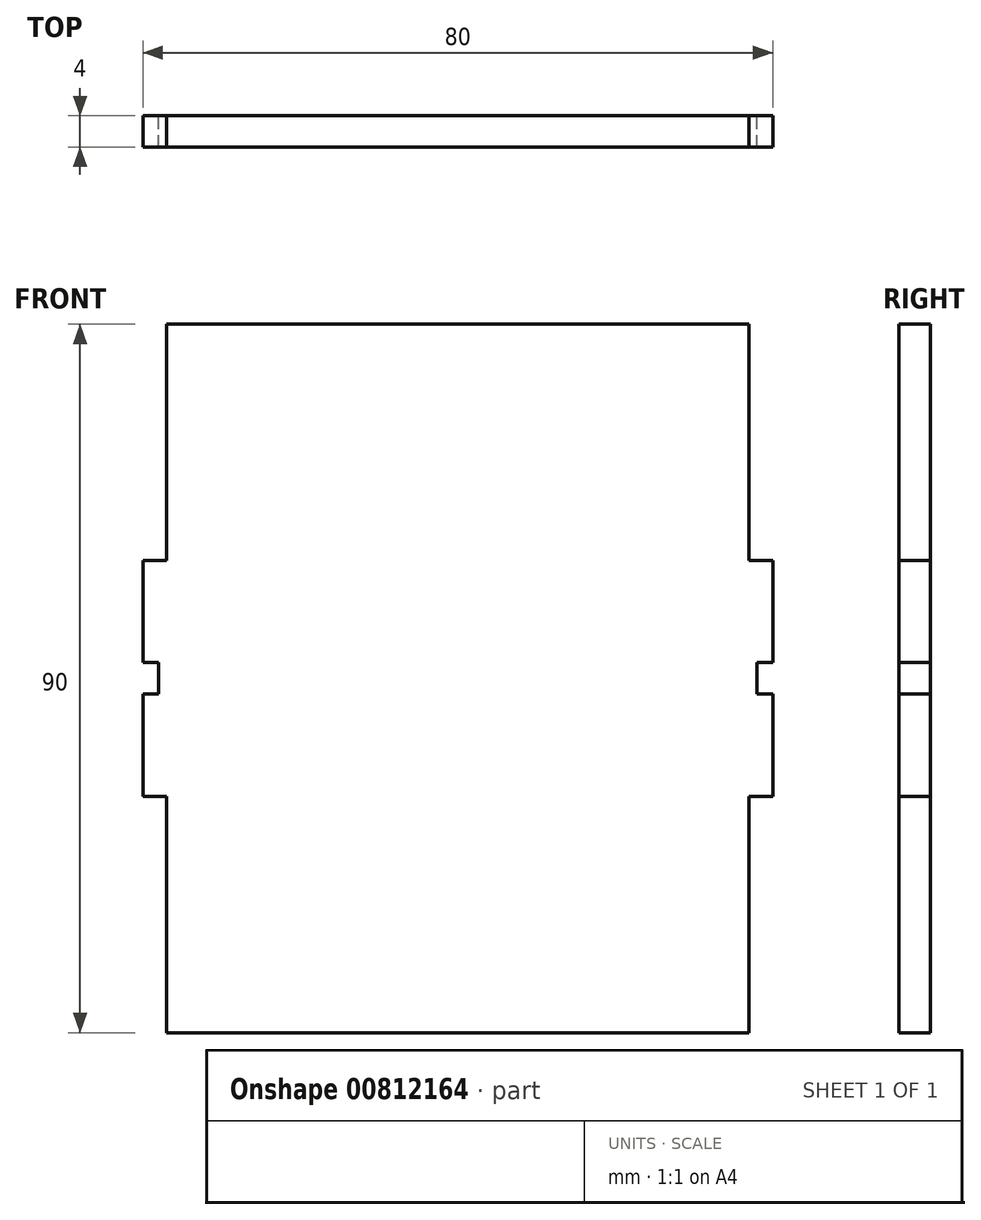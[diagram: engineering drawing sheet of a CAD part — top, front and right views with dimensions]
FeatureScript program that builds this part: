
annotation { "Feature Type Name" : "Feature", "Feature Type Description" : "" }
export const myFeature = defineFeature(function(context is Context, id is Id, definition is map)
    precondition{}
    {
        {
            var Q0;
            Q0=qCreatedBy(makeId("Front.planeOp"),FACE);
            var sketch = newSketch(context, id + "F0", { "sketchPlane" : qUnion([Q0])});
            skLineSegment(sketch, "E0", {"start": v(40, 2) * mm, "end": v(40, 15) * mm});
            skLineSegment(sketch, "E1", {"start": v(37, 45) * mm, "end": v(-37, 45) * mm});
            skLineSegment(sketch, "E2", {"start": v(-40, 15) * mm, "end": v(-40, 2) * mm});
            skLineSegment(sketch, "E3", {"start": v(-37, -45) * mm, "end": v(37, -45) * mm});
            skLineSegment(sketch, "E4", {"start": v(40, -15) * mm, "end": v(40, -2) * mm});
            skLineSegment(sketch, "E5.0", {"start": v(37, 15) * mm, "end": v(40, 15) * mm});
            skLineSegment(sketch, "E6.0", {"start": v(37, -15) * mm, "end": v(40, -15) * mm});
            skLineSegment(sketch, "E7.MirrorCS", {"start": v(37, 15) * mm, "end": v(37, 45) * mm});
            skLineSegment(sketch, "E8.MirrorCS", {"start": v(37, -15) * mm, "end": v(37, -45) * mm});
            skLineSegment(sketch, "E9.0", {"start": v(38, -2) * mm, "end": v(40, -2) * mm});
            skLineSegment(sketch, "E10.0", {"start": v(38, -2) * mm, "end": v(38, 0) * mm});
            skLineSegment(sketch, "E11.MirrorCS", {"start": v(38, 2) * mm, "end": v(38, 0) * mm});
            skLineSegment(sketch, "E12.MirrorCS", {"start": v(38, 2) * mm, "end": v(40, 2) * mm});
            skPoint(sketch, "E13.start.orphan", {"position": v(0, 0) * mm});
            skLineSegment(sketch, "E14.MirrorCS", {"start": v(-37, 15) * mm, "end": v(-40, 15) * mm});
            skLineSegment(sketch, "E15.MirrorCS", {"start": v(-37, -15) * mm, "end": v(-40, -15) * mm});
            skLineSegment(sketch, "E16.MirrorCS", {"start": v(-38, 2) * mm, "end": v(-40, 2) * mm});
            skLineSegment(sketch, "E17.MirrorCS", {"start": v(-38, -2) * mm, "end": v(-40, -2) * mm});
            skLineSegment(sketch, "E18.MirrorCS", {"start": v(-38, -2) * mm, "end": v(-38, 0) * mm});
            skLineSegment(sketch, "E19.MirrorCS", {"start": v(-38, 2) * mm, "end": v(-38, 0) * mm});
            skLineSegment(sketch, "E20.MirrorCS", {"start": v(-40, 2) * mm, "end": v(-40, 15) * mm});
            skLineSegment(sketch, "E21.MirrorCS", {"start": v(-40, -15) * mm, "end": v(-40, -2) * mm});
            skLineSegment(sketch, "E22.MirrorCS", {"start": v(-37, -15) * mm, "end": v(-37, -45) * mm});
            skLineSegment(sketch, "E23.MirrorCS", {"start": v(-37, 15) * mm, "end": v(-37, 45) * mm});
            skLineSegment(sketch, "E24.trimOffspring", {"start": v(-40, -2) * mm, "end": v(-40, -15) * mm});
            skSolve(sketch);
        }
        {
            var Q0;
            Q0 = qSketchRegion(id + "F0", true);
            extrude(context, id + "F1", {"entities" : qUnion([Q0]), "depth" : 4 * mm, "offsetDistance" : 25 * mm});
        }
    });
